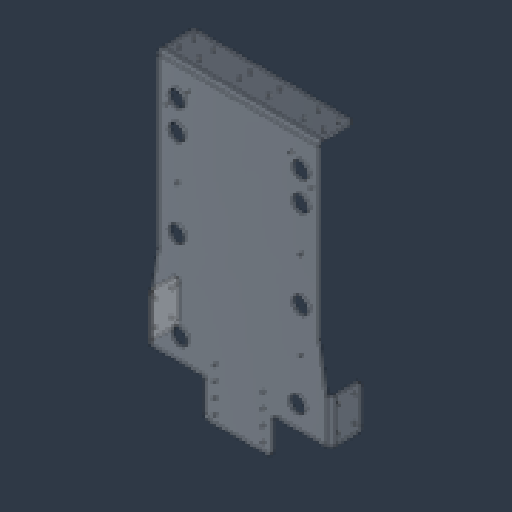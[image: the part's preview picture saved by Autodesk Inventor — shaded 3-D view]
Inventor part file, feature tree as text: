
AUTODESK INVENTOR PART (.ipt)
format: ipt  version: 2024.3 (Build 283343000, 343)  size: 418,304 bytes
history: native  units: in
note: dims shown in document units (in); Inventor stores cm internally (conversion verified against a paired STEP export)
features: sketch x11, sheet_metal_op x9, hole x7, other x5, mirror x4, projected_geometry x2, chamfer x1
ambient origin geometry x8: Origin, YZ Plane, XZ Plane, XY Plane, X Axis, Y Axis, Z Axis, Center Point
bodies: Solid1 (feature_tree)
feature tree (39):
  sheet_metal_op  "Face1"
  hole  "Hole1"  [1 undecoded]
  sheet_metal_op  "Flange1"
  hole  "Hole2"  [1 undecoded]
  hole  "Hole3"  [1 undecoded]
  hole  "Hole4"  [1 undecoded]
  mirror  "Mirror1"
  mirror  "Mirror2"
  sheet_metal_op  "Face3"
  sheet_metal_op  "Flange3"
  hole  "Hole6"  [1 undecoded]
  hole  "Hole7"  [1 undecoded]
  mirror  "Mirror3"
  hole  "Hole8"  [1 undecoded]
  mirror  "Mirror4"
  chamfer  "Corner Round1"
  sketch  "Sketch1"  dims[d0=11.0in d1=17.5in]
  other  "Plate1"
  sketch  "Sketch2"  dims[d2=0.1875in d3=8.5in]
  sketch  "Sketch3"  dims[d4=4.0in]
  other  "Plate2"
  sheet_metal_op  "Bend1"
  sheet_metal_op  "Corner1"
  sketch  "Sketch4"  dims[d5=1.125in d6=0.75in d7=0.385in d8=0.25in d9=0.5635in d10=0.1875in d11=0.8108in]
  projected_geometry  "Projected Loop1"
  sketch  "Sketch5"  dims[d12=0.7874in d14=6.01in d15=0.3937in d17=1.0in d22=0.1875in]
  projected_geometry  "Projected Loop2"
  sketch  "Sketch9"  dims[d23=0.0938in d24=0.375in]
  sketch  "Sketch12"  dims[d25=0.1875in d26=2.3125in d27=90.0deg d28=0.1875in]
  other  "Plate5"
  sheet_metal_op  "Bend4"
  sketch  "Sketch13"  dims[d29=0.75in d30=0.1875in]
  other  "Plate6"
  sheet_metal_op  "Bend5"
  sheet_metal_op  "Corner3"
  sketch  "Sketch14"  dims[d31=0.1875in]
  sketch  "Sketch15"  dims[d33=4.5in]
  sketch  "Sketch16"  dims[d34=4.5in d35=0.7874in d37=0.75in d38=0.3937in d40=1.0in d42=0.201in d43=0.75in d44=0.385in d45=0.25in d46=0.5635in d47=1.0in d48=0.8108in d53=-1.0in d54=0.201in d55=0.75in d56=0.375in d57=0.25in d58=0.5635in d59=1.0in d60=0.8108in d61=0.625in d76=4.5in d77=3.5in d87=0.159in d88=0.75in d89=0.375in d90=0.25in d91=0.5635in d92=0.1875in d93=0.8108in d107=2.5in d108=4.625in d109=0.1875in d110=0.1875in d111=0.0938in d112=0.375in d113=0.1875in d114=0.5in d115=3.0in d117=6.0in d118=0.1875in d119=0.0938in d120=0.375in d121=0.1875in d122=2.1875in d123=90.0deg d124=0.1875in d125=0.75in d126=0.1875in d127=0.1875in d130=0.625in d131=1.75in d132=1.125in d133=0.625in d134=0.201in d135=0.75in d136=0.375in d137=0.25in d138=0.5635in d139=0.1875in d140=0.8108in d141=0.5625in d143=1.0in d144=1.375in d146=0.201in d147=0.75in d148=0.375in d149=0.25in d150=0.5635in d151=1.0in d152=0.8108in d153=0.5625in d154=0.6875in d155=0.5in d156=4.0in d157=0.1772in d158=0.75in d159=0.375in d160=0.25in d161=0.5635in d162=0.1875in d163=0.8108in d164=6.01in d165=0.6322in d166=6.01in d167=0.6047in d192=2.01in d193=2.0in d194=45.0deg d195=0.25in]
  other  "Definition1"
note: 7 required parameter values undecoded (feature->parameter linkage not recoverable at this tier; creation-order binding heuristic only, values carry confidence <= 0.55)
